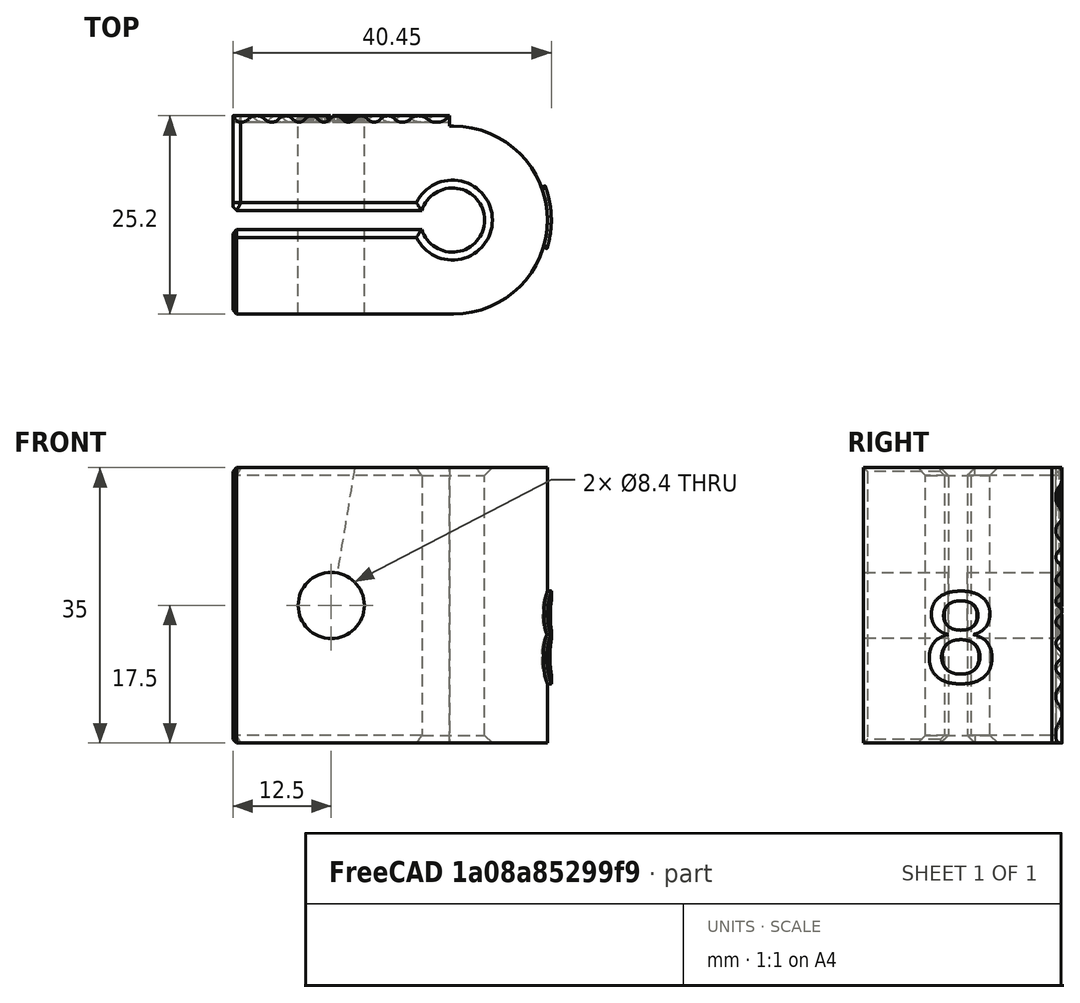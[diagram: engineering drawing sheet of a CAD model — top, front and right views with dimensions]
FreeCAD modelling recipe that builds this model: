
FCSTD DOCUMENT  (FreeCAD 1.1R44225 (Git))
Label: Bar-to-bar clamp
License: All rights reserved
LicenseURL: https://en.wikipedia.org/wiki/All_rights_reserved
objects: Part::FeaturePython×3, Sketcher::SketchObject×3, App::Point×2, PartDesign::Body×2, Spreadsheet::Sheet×1, Part::RuledSurface×1, Part::Extrusion×1, Part::Box×1, Part::MultiCommon×1, Part::Part2DObjectPython×1, Part::Cylinder×1, PartDesign::Pad×1, PartDesign::FeatureBase×1, Part::MultiFuse×1, Part::Cut×1, Part::Chamfer×1
note: 25 computed .brp shape members not serialized (recipe doc carries the construction recipe); baked Part::Feature solids carry a one-line shape summary decoded from their .brp

FEATURE [Spreadsheet::Sheet] Spreadsheet  label="Parameters"
  cells = A1='Description of parameter; B1='Measurement; A2='Bolt diameter (mm); B2(bolt)=8; A3='Bolt diameter tolerance (mm); B3(BoltTolerance)=0.4; A4='Rod diameter (mm); B4(rod)=8; A5='Rod diameter tolerance (mm); B5(RodTolerance)=0.15; A7='Interface parameters; A8='Inner radius; B8(InnerRadius)=2; A9='Outer radius; B9(OuterRadius)=25; A10='Amplitude of waves; B10(amplitude)=0.8; A11='Number of waves; B11(NumberOfWaves)=36; A12='Interval (do not change); B12(Interval)=0.01
FEATURE [Part::FeaturePython] ParametricCurve  # WARN: FeaturePython — macro-defined, semantics opaque (R4)
  AttacherType = Attacher::AttachEngine3D
  Closed = false
  Continuity = C2
  EditFormulas = false
  F_X = 0
  F_Y = 0
  F_Z = 0
  F_a = 25
  F_b = 36
  F_c = 0.8
  F_d = [0,0]
  FormulaName = formula1
  Formulas = 0
  Interval = 0.01
  MakeFace = false
  PlusOneIteration = true
  Points = (630) [(25,0,0.4),(24.9988,0.249996,0.602621),(24.995,0.499967,0.738292),(24.9888,0.749888,0.791969),(24.98,0.999733,0.799956),(24.9688,1.24948,0.799593),+624 more]
  ShapeType = 0
  Sorted = false
  UpdateSpreadsheet = false
  UseSpreadsheet = false
  Version = 2023.05.06
  X = a*cos(t)
  Y = a*sin(t)
  Z = c * ( 3*((1 + sin(b*t))/2)^2 - 2*((1 + sin(b*t))/2)^3 )
  a = 25
  b = 36
  c = 0.8
  t_max = 6.28319
  t_min = 0
  expr: Interval = .Spreadsheet.Interval
  expr: a = .Spreadsheet.OuterRadius
  expr: b = .Spreadsheet.NumberOfWaves
  expr: c = .Spreadsheet.amplitude
FEATURE [Part::FeaturePython] ParametricCurve001  # WARN: FeaturePython — macro-defined, semantics opaque (R4)
  AttacherType = Attacher::AttachEngine3D
  Closed = false
  Continuity = C2
  EditFormulas = false
  F_X = 0
  F_Y = 0
  F_Z = 0
  F_a = 2
  F_b = 36
  F_c = 0.8
  F_d = [0,0]
  FormulaName = formula2
  Formulas = 0
  Interval = 0.01
  MakeFace = false
  PlusOneIteration = true
  Points = (630) [(2,0,0.4),(1.9999,0.0199997,0.602621),(1.9996,0.0399973,0.738292),(1.9991,0.059991,0.791969),(1.9984,0.0799787,0.799956),(1.9975,0.0999583,0.799593),+624 more]
  ShapeType = 0
  Sorted = false
  UpdateSpreadsheet = false
  UseSpreadsheet = false
  Version = 2023.05.06
  X = a*cos(t)
  Y = a*sin(t)
  Z = c * ( 3*((1 + sin(b*t))/2)^2 - 2*((1 + sin(b*t))/2)^3 )
  a = 2
  b = 36
  c = 0.8
  t_max = 6.28319
  t_min = 0
  expr: Interval = .Spreadsheet.Interval
  expr: a = .Spreadsheet.InnerRadius
  expr: b = .Spreadsheet.NumberOfWaves
  expr: c = .Spreadsheet.amplitude
FEATURE [Part::RuledSurface] Ruled_Surface
  Curve1 = -> ParametricCurve [Edge1]
  Curve2 = -> ParametricCurve001 [Edge1]
  Orientation = 0
  Placement = pos=(10,-3.75,-17.5) rot=(0.020938,0.999562,0.020938;1.57123rad)
FEATURE [Part::Extrusion] Extrude003
  Base = -> Ruled_Surface
  Dir = (-1,0,0)
  DirMode = 0
  FaceMakerClass = Part::FaceMakerBullseye
  FaceMakerMode = 3
  LengthFwd = 2
  LengthRev = 0
  Placement = pos=(7e-15,-0.879345,0.597287) rot=(1,0,0;0.122173rad)
  Solid = false
  Symmetric = false
FEATURE [Part::Box] Box  label="Cube"
  AttacherType = Attacher::AttachEngine3D
  Height = 1.5
  Length = 35
  Placement = pos=(9.4513,-15,0) rot=(0,1,0;1.5708rad)
  Width = 27.5
FEATURE [Part::MultiCommon] Common
  Placement = pos=(0,0,0) rot=(0,1,0;3.14159rad)
  Shapes = -> [Box,Extrude003]
FEATURE [Part::Part2DObjectPython] ShapeString  # Draft 2D object (typed FeaturePython)
  FontFile = <path>
  Fuse = false
  Justification = 4
  JustificationReference = 0
  KeepLeftMargin = false
  MakeFace = true
  ObliqueAngle = 0
  Placement = pos=(30,4.85425,0) rot=(0,0,1;0rad)
  ScaleToSize = true
  Size = 16
  String = 8
  Tracking = 0
FEATURE [Part::Cylinder] Cylinder
  Angle = 360
  AttacherType = Attacher::AttachEngine3D
  FirstAngle = 0
  Height = 30
  Placement = pos=(-15,-2.5,-17.5) rot=(0,1,0;1.5708rad)
  Radius = 4.2
  SecondAngle = 0
  expr: Radius = (Spreadsheet.bolt + Spreadsheet.BoltTolerance) / 2
FEATURE [Sketcher::SketchObject] Sketch
  ArcFitTolerance = 1e-06
  AttachmentSupport = -> [Origin]
  ExternalTypes = [0]
  FullyConstrained = true
  MakeInternals = false
  MapMode = 5
  expr: Constraints[16] = (Spreadsheet.rod + Spreadsheet.RodTolerance) / 2
  sketch-geometry (8):
    g0: LineSegment StartX=-11.95 StartY=-15 StartZ=0 EndX=-11.95 EndY=13 EndZ=0
    g1: LineSegment StartX=-11.95 StartY=-15 StartZ=0 EndX=-1.2 EndY=-15 EndZ=0
    g2: LineSegment StartX=-1.2 StartY=-15 StartZ=0 EndX=-1.2 EndY=9 EndZ=0
    g3: LineSegment StartX=1.2 StartY=9 StartZ=0 EndX=1.2 EndY=-15 EndZ=0
    g4: LineSegment StartX=1.2 StartY=-15 StartZ=0 EndX=11.95 EndY=-15 EndZ=0
    g5: LineSegment StartX=11.95 StartY=-15 StartZ=0 EndX=11.95 EndY=13 EndZ=0
    g6: ArcOfCircle CenterX=-3e-16 CenterY=13 CenterZ=0 NormalX=0 NormalY=0 NormalZ=1 AngleXU=0 Radius=11.95 StartAngle=6.28319 EndAngle=9.42478
    g7: ArcOfCircle CenterX=-2.2e-15 CenterY=12.8943 CenterZ=0 NormalX=0 NormalY=0 NormalZ=1 AngleXU=0 Radius=4.075 StartAngle=5.0113 EndAngle=10.6967
  constraints (26):
    c: Vertical(g0)
    c: Coincident(g0,g1)
    c: Horizontal(g1)
    c: Coincident(g1,g2)
    c: Vertical(g3)
    c: Coincident(g3,g4)
    c: Horizontal(g4)
    c: Coincident(g4,g5)
    c: Vertical(g5)
    c: Coincident(g0,g6)
    c: Coincident(g6,g5)
    c: DistanceY(g3,g-1) = 15
    c: DistanceY(g1,g-1) = 15
    c: Coincident(g3,g7)
    c: Vertical(g2)
    c: Coincident(g7,g2)
    c: Radius(g7) = 4.075
    c: DistanceY(g2,g3) = 0
    c: DistanceY(g3,g3) = 24
    c: DistanceY(g5,g0) = 0
    c: DistanceY(g4,g5) = 28
    c: DistanceX(g4,g4) = 10.75
    c: Equal(g1,g4)
    c: Distance(g1,g-2) = 1.2
    c: Distance(g3,g-2) = 1.2
    c: Radius(g6) = 11.95
FEATURE [PartDesign::Pad] Pad
  Direction = (0,0,1)
  Length = 35
  Length2 = 10
  Profile = -> Sketch
  ReferenceAxis = -> Sketch [N_Axis]
  Refine = true
  Reversed = true
  SideType = 0
  Suppressed = false
  Type = 0
  Type2 = 0
FEATURE [Sketcher::SketchObject] Mapped_Sketch
  ArcFitTolerance = 1e-06
  AttachmentSupport = -> [Pad]
  ExternalTypes = [0]
  FullyConstrained = false
  MakeInternals = false
  Placement = pos=(3.03142,5.20342,0) rot=(0,0,1;0rad)
  sketch-geometry (8):
    g0: LineSegment [constr] StartX=0 StartY=0 StartZ=0 EndX=27.0812 EndY=0 EndZ=0
    g1: LineSegment [constr] StartX=27.0812 StartY=0 StartZ=0 EndX=27.0812 EndY=30 EndZ=0
    g2: LineSegment [constr] StartX=27.0812 StartY=30 StartZ=0 EndX=0 EndY=30 EndZ=0
    g3: LineSegment [constr] StartX=0 StartY=30 StartZ=0 EndX=0 EndY=0 EndZ=0
    g4: LineSegment [constr] StartX=10.2789 StartY=6.24604 StartZ=0 EndX=10.2789 EndY=-19.2688 EndZ=0
    g5: LineSegment [constr] StartX=10.2789 StartY=-19.2688 StartZ=0 EndX=52.8869 EndY=-19.2688 EndZ=0
    g6: LineSegment [constr] StartX=52.8869 StartY=-19.2688 StartZ=0 EndX=52.8869 EndY=6.24604 EndZ=0
    g7: LineSegment [constr] StartX=52.8869 StartY=6.24604 StartZ=0 EndX=10.2789 EndY=6.24604 EndZ=0
  constraints (19):
    c: Coincident(g0,g-1)
    c: Coincident(g0,g1)
    c: Coincident(g1,g2)
    c: Coincident(g2,g3)
    c: Coincident(g3,g0)
    c: Horizontal(g0)
    c: Horizontal(g2)
    c: Vertical(g1)
    c: Vertical(g3)
    c: DistanceX(g2,g2) = 27.0812
    c: DistanceY(g1,g1) = 30
    c: Coincident(g4,g5)
    c: Coincident(g5,g6)
    c: Coincident(g6,g7)
    c: Coincident(g7,g4)
    c: Vertical(g4)
    c: Vertical(g6)
    c: Horizontal(g5)
    c: Horizontal(g7)
FEATURE [App::Point] Origin001
  Role = Origin
FEATURE [Part::FeaturePython] Sketch_On_Surface  # WARN: FeaturePython — macro-defined, semantics opaque (R4)
  ConstructionBounds = true
  ExtraObjects = -> [ShapeString]
  FillExtrusion = true
  FillFaces = true
  ReverseU = false
  ReverseV = false
  Sketch = -> Mapped_Sketch
  SwapUV = false
  Thickness = 0.5
FEATURE [PartDesign::FeatureBase] Clone001
  BaseFeature = -> Common
  Placement = pos=(0.0566779,0,-30) rot=(0,0,0;3.14159rad)
  Suppressed = false
FEATURE [App::Point] Origin005
  Role = Origin
FEATURE [PartDesign::Body] Body002  label="Interface 2"
  AllowCompound = false
  Group = -> [Clone001]
  Origin = -> Origin004
  Placement = pos=(-2.5,3.47e-14,-5) rot=(0,0,1;0rad)
  Tip = -> Clone001
FEATURE [Sketcher::SketchObject] Sketch001
  ArcFitTolerance = 1e-06
  AttachmentSupport = -> [Pad]
  ExternalTypes = [0]
  FullyConstrained = true
  MakeInternals = false
  MapMode = 5
  Placement = pos=(11.95,0,0) rot=(0.57735,0.57735,0.57735;2.0944rad)
  sketch-geometry (7):
    g0: LineSegment StartX=-2.5 StartY=-9.9 StartZ=0 EndX=-9.08179 EndY=-13.7 EndZ=0
    g1: LineSegment StartX=-9.08179 StartY=-13.7 StartZ=0 EndX=-9.08179 EndY=-21.3 EndZ=0
    g2: LineSegment StartX=-9.08179 StartY=-21.3 StartZ=0 EndX=-2.5 EndY=-25.1 EndZ=0
    g3: LineSegment StartX=-2.5 StartY=-25.1 StartZ=0 EndX=4.08179 EndY=-21.3 EndZ=0
    g4: LineSegment StartX=4.08179 StartY=-21.3 StartZ=0 EndX=4.08179 EndY=-13.7 EndZ=0
    g5: LineSegment StartX=4.08179 StartY=-13.7 StartZ=0 EndX=-2.5 EndY=-9.9 EndZ=0
    g6: Circle [constr] CenterX=-2.5 CenterY=-17.5 CenterZ=0 NormalX=0 NormalY=0 NormalZ=1 AngleXU=0 Radius=7.6
  constraints (17):
    c: Coincident(g0,g1)
    c: Coincident(g1,g2)
    c: Coincident(g2,g3)
    c: Coincident(g3,g4)
    c: Coincident(g4,g5)
    c: Coincident(g5,g0)
    c: Equal(g0, g1-g5) x5
    c: PointOnObject(g0,g6)
    c: PointOnObject(g1,g6)
    c: PointOnObject(g2,g6)
    c: PointOnObject(g3,g6)
    c: PointOnObject(g4,g6)
    c: PointOnObject(g5,g6)
    c: Distance(g0,g-2) = 2.5
    c: Distance(g2,g-2) = 2.5
    c: DistanceY(g6,g-1) = 17.5
    c: DistanceY(g2,g0) = 15.2
FEATURE [PartDesign::Body] Body  label="Main clamp body"
  AllowCompound = false
  Group = -> [Sketch,Pad,Sketch001]
  Origin = -> Origin
  Tip = -> Pad
FEATURE [Part::MultiFuse] Fusion
  Shapes = -> [Body,Sketch_On_Surface,Body002]
FEATURE [Part::Cut] Cut
  Base = -> Fusion
  Tool = -> Cylinder
FEATURE [Part::Chamfer] Chamfer
  Base = -> Cut
  EdgeLinks = -> Cut [Edge3,Edge4,Edge5,Edge6,Edge7,Edge9,Edge10,Edge11,Edge13,Edge19,Edge20,Edge26,Edge27]
  Edges = 13 edges: [Edge3 r=1,Edge4 r=1,Edge5 r=1,Edge6 r=1,Edge7 r=0.5,Edge9 r=0.5,Edge10 r=1,Edge11 r=1,Edge13 r=1,Edge19 r=0.5,Edge20 r=1,Edge26 r=0.5,Edge27 r=0.5]
  Placement = pos=(0,0,0) rot=(0,0,1;4.71239rad)
note: 1 file-system path scrubbed to <path> (originals preserved in the JSON sidecar)
